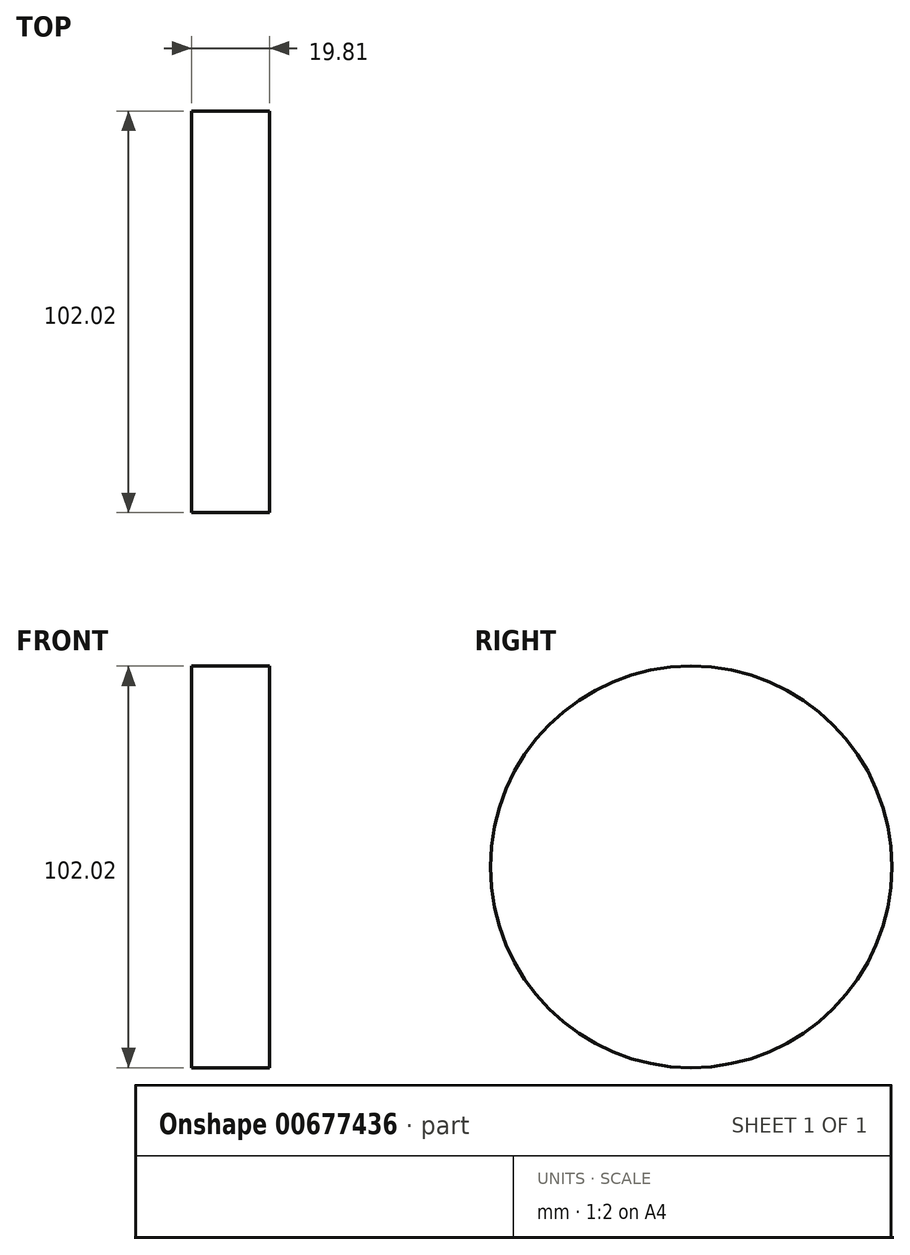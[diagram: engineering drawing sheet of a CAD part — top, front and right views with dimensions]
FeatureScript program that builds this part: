
annotation { "Feature Type Name" : "Feature", "Feature Type Description" : "" }
export const myFeature = defineFeature(function(context is Context, id is Id, definition is map)
    precondition{}
    {
        {
            var Q0;
            Q0=qCreatedBy(makeId("Right.planeOp"),FACE);
            var sketch = newSketch(context, id + "F0", { "sketchPlane" : qUnion([Q0])});
            skCircle(sketch, "E0", {"center": v(0, 0) * mm, "radius": 51.01 * mm});
            skSolve(sketch);
        }
        {
            var Q0;
            Q0=sQuery(id+"F0.wireOp",EDGE,"E0");
            extrude(context, id + "F1", {"bodyType" : ToolBodyType.SURFACE, "surfaceEntities" : qUnion([Q0]), "depth" : 19.8 * mm, "offsetDistance" : 25.4 * mm});
        }
    });
